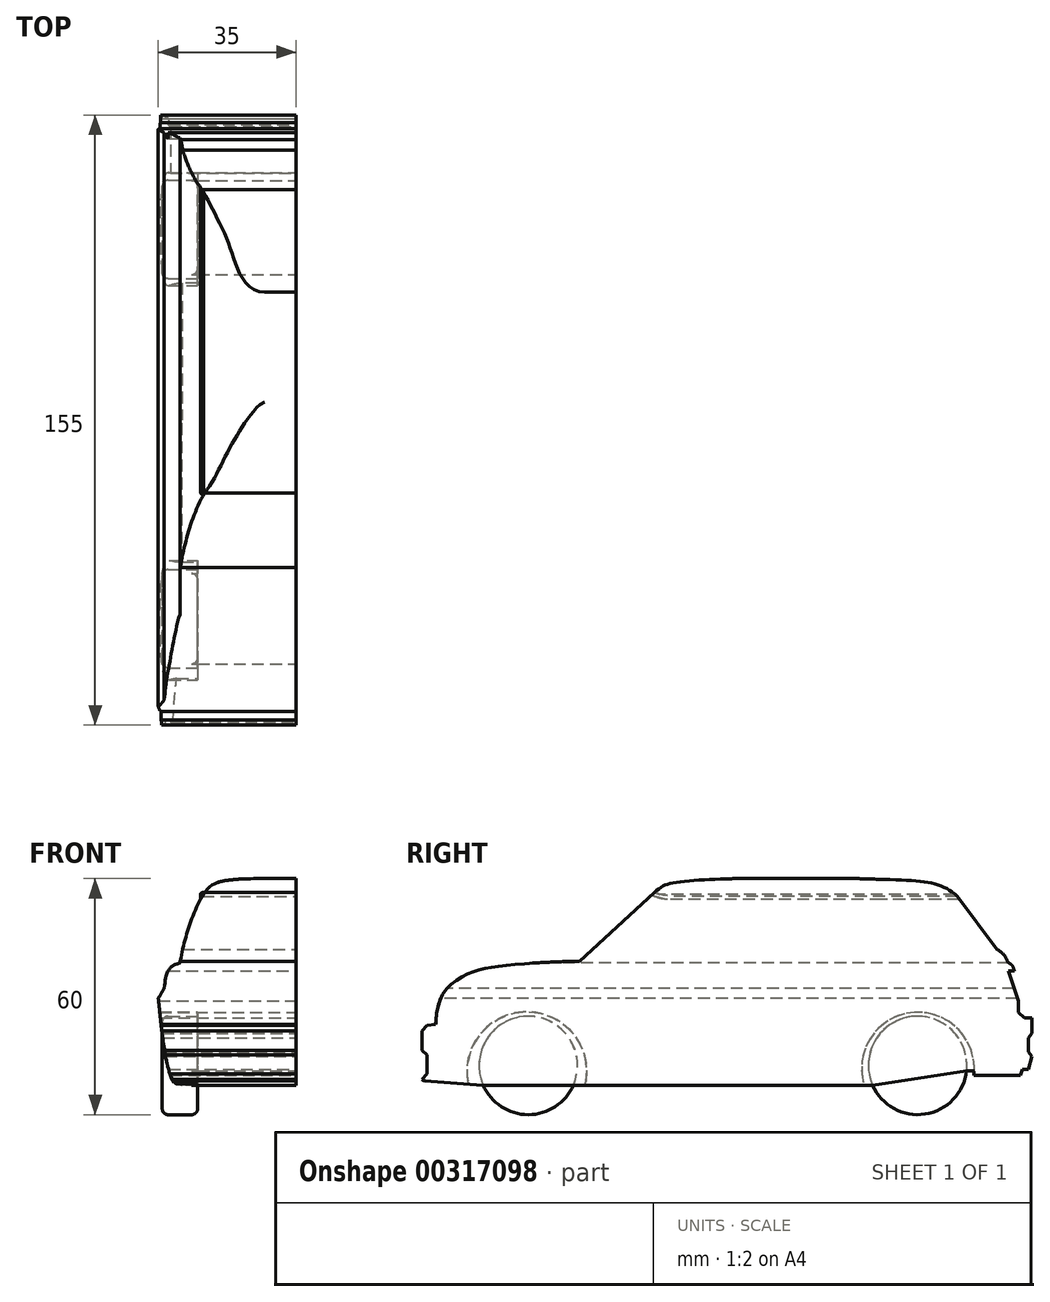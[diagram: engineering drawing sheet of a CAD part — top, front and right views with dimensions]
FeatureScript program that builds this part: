
annotation { "Feature Type Name" : "Feature", "Feature Type Description" : "" }
export const myFeature = defineFeature(function(context is Context, id is Id, definition is map)
    precondition{}
    {
        {
            var Q0;
            Q0=qCreatedBy(makeId("Right.planeOp"),FACE);
            var sketch = newSketch(context, id + "F0", { "sketchPlane" : qUnion([Q0])});
            skLineSegment(sketch, "E0.bottom", {"start": v(-77.5, 0) * mm, "end": v(77.5, 0) * mm});
            skLineSegment(sketch, "E0.top", {"start": v(-77.5, 60) * mm, "end": v(77.5, 60) * mm});
            skLineSegment(sketch, "E0.left", {"start": v(-77.5, 0) * mm, "end": v(-77.5, 60) * mm});
            skLineSegment(sketch, "E0.right", {"start": v(77.5, 0) * mm, "end": v(77.5, 60) * mm});
            skPoint(sketch, "E1", {"position": v(74.5, 10) * mm});
            skPoint(sketch, "E2", {"position": v(75, 11.5) * mm});
            skLineSegment(sketch, "E3", {"start": v(74.5, 10) * mm, "end": v(75, 11.5) * mm});
            skLineSegment(sketch, "E4", {"start": v(76.5, 11.5) * mm, "end": v(75, 11.5) * mm});
            skLineSegment(sketch, "E5", {"start": v(76.5, 11.5) * mm, "end": v(77.5, 14.85) * mm});
            skLineSegment(sketch, "E6", {"start": v(77.5, 14.85) * mm, "end": v(76.5, 16) * mm});
            skLineSegment(sketch, "E7", {"start": v(76.5, 16) * mm, "end": v(76.5, 19.5) * mm});
            skLineSegment(sketch, "E8", {"start": v(76.5, 19.5) * mm, "end": v(77.5, 20.62) * mm});
            skLineSegment(sketch, "E9", {"start": v(77.5, 20.62) * mm, "end": v(77.5, 24.62) * mm});
            skLineSegment(sketch, "E10", {"start": v(77.5, 24.62) * mm, "end": v(75.5, 24.62) * mm});
            skLineSegment(sketch, "E11", {"start": v(75.5, 24.62) * mm, "end": v(74, 25.94) * mm});
            skLineSegment(sketch, "E12", {"start": v(74, 25.94) * mm, "end": v(74, 28.94) * mm});
            skPoint(sketch, "E13", {"position": v(71.5, 36.54) * mm});
            skLineSegment(sketch, "E14", {"start": v(71.5, 36.54) * mm, "end": v(74, 28.94) * mm});
            skLineSegment(sketch, "E15", {"start": v(71.5, 36.54) * mm, "end": v(73, 36.54) * mm});
            skFitSpline(sketch, "E16", {"points": [v(73, 36.54) * mm, v(72.46, 37.9) * mm, v(71.27, 38.84) * mm], "startDerivative": vector(-0.98, 3.1) * mm, "endDerivative": vector(-3.68, 3.33) * mm});
            skPoint(sketch, "E17", {"position": v(68.5, 42) * mm});
            skFitSpline(sketch, "E18", {"points": [v(71.27, 38.84) * mm, v(70.34, 40.67) * mm, v(68.5, 42) * mm], "startDerivative": vector(-1.5, 4.04) * mm, "endDerivative": vector(-4.02, 2.3) * mm});
            skPoint(sketch, "E19", {"position": v(58.5, 55.5) * mm});
            skLineSegment(sketch, "E20", {"start": v(58.5, 55.5) * mm, "end": v(68.5, 42) * mm});
            skPoint(sketch, "E21", {"position": v(32.5, 60) * mm});
            skFitSpline(sketch, "E22", {"points": [v(32.5, 60) * mm, v(52.32, 58.74) * mm, v(58.5, 55.5) * mm], "startDerivative": vector(47.26, -1.79) * mm, "endDerivative": vector(14.98, -13.72) * mm});
            skPoint(sketch, "E23", {"position": v(4.5, 60) * mm});
            skPoint(sketch, "E24", {"position": v(-18.5, 56.5) * mm});
            skFitSpline(sketch, "E25", {"points": [v(4.5, 60) * mm, v(-13.58, 58.93) * mm, v(-18.5, 56.5) * mm], "startDerivative": vector(-24.6, -0.14) * mm, "endDerivative": vector(-14.76, -12.16) * mm});
            skFitSpline(sketch, "E26", {"points": [v(58.5, 55.5) * mm, v(-13.58, 55.5) * mm, v(-18.5, 56.5) * mm], "startDerivative": vector(-273.31, 0) * mm, "endDerivative": vector(-35.98, 14.37) * mm});
            skLineSegment(sketch, "E27", {"start": v(-18.5, 56.5) * mm, "end": v(-37.5, 39) * mm});
            skPoint(sketch, "E28", {"position": v(-74, 23) * mm});
            skFitSpline(sketch, "E29", {"points": [v(-37.5, 39) * mm, v(-58.13, 37.7) * mm, v(-66.06, 35.68) * mm, v(-72.37, 30.31) * mm, v(-74, 23) * mm], "startDerivative": vector(-69.68, -1.64) * mm, "endDerivative": vector(-0.32, -25.11) * mm});
            skLineSegment(sketch, "E30", {"start": v(-74, 23) * mm, "end": v(-76.26, 22.64) * mm});
            skLineSegment(sketch, "E31", {"start": v(-76.26, 22.64) * mm, "end": v(-77.5, 21.31) * mm});
            skLineSegment(sketch, "E32", {"start": v(-77.5, 21.31) * mm, "end": v(-77.5, 16.31) * mm});
            skLineSegment(sketch, "E33", {"start": v(-77.5, 16.31) * mm, "end": v(-76.26, 15.16) * mm});
            skPoint(sketch, "E34", {"position": v(-77.5, 9) * mm});
            skLineSegment(sketch, "E35", {"start": v(-77.5, 9) * mm, "end": v(-76.26, 10.33) * mm});
            skLineSegment(sketch, "E36", {"start": v(-76.26, 10.33) * mm, "end": v(-76.26, 15.16) * mm});
            skLineSegment(sketch, "E37", {"start": v(-77.5, 9) * mm, "end": v(-76.88, 8.62) * mm});
            skPoint(sketch, "E37.endSnap0", {"position": v(-76.88, 9.67) * mm});
            skLineSegment(sketch, "E38", {"start": v(-61.96, 7.5) * mm, "end": v(-76.88, 8.62) * mm});
            skLineSegment(sketch, "E39", {"start": v(-39.04, 7.5) * mm, "end": v(36.96, 7.5) * mm});
            skArc(sketch, "E40", {"start": v(-36.04, 7.5) * mm, "mid": v(-50.7, 26.13) * mm, "end": v(-65.7, 7.78) * mm});
            skPoint(sketch, "E41.second.point", {"position": v(48.41, 0) * mm});
            skPoint(sketch, "E41.third.point", {"position": v(52.15, 24.43) * mm});
            skLineSegment(sketch, "E42", {"start": v(74.5, 10) * mm, "end": v(62.7, 10) * mm});
            skArc(sketch, "E43", {"start": v(62.7, 10) * mm, "mid": v(47.2, 25.95) * mm, "end": v(34.8, 7.5) * mm});
            skLineSegment(sketch, "E44", {"start": v(62.79, 11.13) * mm, "end": v(60.84, 11.13) * mm});
            skFitSpline(sketch, "E45", {"points": [v(-37.5, 39) * mm, v(68.5, 42) * mm], "startDerivative": vector(22.88, -2.64) * mm, "endDerivative": vector(106, 3) * mm});
            skPoint(sketch, "E46", {"position": v(-28, 38.86) * mm});
            skFitSpline(sketch, "E47", {"points": [v(59.1, 54.7) * mm, v(-13.74, 54.51) * mm, v(-19.24, 55.82) * mm], "startDerivative": vector(-279.36, -0.7) * mm, "endDerivative": vector(-40.33, 16.33) * mm});
            skPoint(sketch, "E48", {"position": v(-13, 54.48) * mm});
            skLineSegment(sketch, "E49", {"start": v(-13, 54.48) * mm, "end": v(-28, 38.86) * mm});
            skLineSegment(sketch, "E50", {"start": v(-22.5, 38.96) * mm, "end": v(-9.5, 54.44) * mm});
            skArc(sketch, "E51", {"start": v(-39.04, 7.5) * mm, "mid": v(-50.5, 24.07) * mm, "end": v(-61.96, 7.5) * mm});
            skArc(sketch, "E52", {"start": v(60.84, 11.13) * mm, "mid": v(46.53, 24.86) * mm, "end": v(36.96, 7.5) * mm});
            skLineSegment(sketch, "E53", {"start": v(60.84, 11.13) * mm, "end": v(36.96, 7.5) * mm});
            skLineSegment(sketch, "E54", {"start": v(-39.04, 7.5) * mm, "end": v(-61.96, 7.5) * mm});
            skSolve(sketch);
        }
        {
            var Q0;
            Q0=makeQuery(id+"F0.imprint","IMPRINT",FACE,{"disambiguationData":[TD([[makeQuery(id+"F0.imprint","IMPRINT",EDGE,{"derivedFrom":sQuery(id+"F0.wireOp",EDGE,"E3")}),1.0]])]});
            var Q1;
            {var subQ0=sQuery(id+"F0.wireOp",EDGE,"E22");Q1=makeQuery(id+"F0.imprint","IMPRINT",FACE,{"disambiguationData":[TD([[makeQuery(id+"F0.imprint","IMPRINT",EDGE,{"derivedFrom":subQ0}),-1.0]])]});}
            var Q2;
            {var subQ0=sQuery(id+"F0.wireOp",EDGE,"E41");var subQ1=makeQuery(id+"F0.imprint","INTERSECT",VERTEX,{"derivedFrom":[sQuery(id+"F0.wireOp",EDGE,"E39"),subQ0]});Q2=makeQuery(id+"F0.imprint","IMPRINT",FACE,{"disambiguationData":[TD([[makeQuery(id+"F0.imprint","IMPRINT",EDGE,{"disambiguationData":[TD([[subQ1,-1.0]])],"derivedFrom":subQ0}),1.0]])]});}
            var Q3;
            {var subQ0=sQuery(id+"F0.wireOp",EDGE,"J8efTKUS-d59Y-iMBA-VsDp-mcbD3HcGddpb");var subQ1=makeQuery(id+"F0.imprint","INTERSECT",VERTEX,{"derivedFrom":[subQ0,sQuery(id+"F0.wireOp",EDGE,"E38")]});Q3=makeQuery(id+"F0.imprint","IMPRINT",FACE,{"disambiguationData":[TD([[makeQuery(id+"F0.imprint","IMPRINT",EDGE,{"disambiguationData":[TD([[subQ1,-1.0]])],"derivedFrom":subQ0}),1.0]])]});}
            var Q4;
            {var subQ5=sQuery(id+"F0.wireOp",EDGE,"E49");Q4=makeQuery(id+"F0.imprint","IMPRINT",FACE,{"disambiguationData":[TD([[makeQuery(id+"F0.imprint","IMPRINT",EDGE,{"derivedFrom":subQ5}),-1.0]])]});}
            var Q5;
            {var subQ0=sQuery(id+"F0.wireOp",EDGE,"E49");Q5=makeQuery(id+"F0.imprint","IMPRINT",FACE,{"disambiguationData":[TD([[makeQuery(id+"F0.imprint","IMPRINT",EDGE,{"derivedFrom":subQ0}),1.0]])]});}
            var Q6;
            {var subQ4=sQuery(id+"F0.wireOp",EDGE,"E26");Q6=makeQuery(id+"F0.imprint","IMPRINT",FACE,{"disambiguationData":[TD([[makeQuery(id+"F0.imprint","IMPRINT",EDGE,{"derivedFrom":subQ4}),1.0]])]});}
            var Q7;
            {var subQ5=sQuery(id+"F0.wireOp",EDGE,"E50");Q7=makeQuery(id+"F0.imprint","IMPRINT",FACE,{"disambiguationData":[TD([[makeQuery(id+"F0.imprint","IMPRINT",EDGE,{"derivedFrom":subQ5}),-1.0]])]});}
            extrude(context, id + "F1", {"entities" : qUnion([Q0, Q1, Q2, Q3, Q4, Q5, Q6, Q7]), "oppositeDirection" : true, "depth" : 35 * mm});
        }
        {
            var Q0;
            Q0=qCreatedBy(makeId("Front.planeOp"),FACE);
            var sketch = newSketch(context, id + "F2", { "sketchPlane" : qUnion([Q0])});
            skLineSegment(sketch, "E55.bottom", {"start": v(0, 0) * mm, "end": v(-35, 0) * mm});
            skLineSegment(sketch, "E55.top", {"start": v(0, 65) * mm, "end": v(-35, 65) * mm});
            skLineSegment(sketch, "E55.left", {"start": v(0, 0) * mm, "end": v(0, 65) * mm});
            skLineSegment(sketch, "E55.right", {"start": v(-35, 0) * mm, "end": v(-35, 65) * mm});
            skPoint(sketch, "E56", {"position": v(-35, 29.5) * mm});
            skLineSegment(sketch, "E57", {"start": v(-35, 29.5) * mm, "end": v(-33.5, 32.1) * mm});
            skFitSpline(sketch, "E58", {"points": [v(-33.5, 32.1) * mm, v(-32.18, 37.03) * mm, v(-29.5, 38.5) * mm], "startDerivative": vector(1.24, 9.06) * mm, "endDerivative": vector(5.03, 0.83) * mm});
            skPoint(sketch, "E59", {"position": v(-23.5, 56) * mm});
            skFitSpline(sketch, "E60", {"points": [v(-23.5, 56) * mm, v(-29.5, 38.5) * mm], "startDerivative": vector(-9.23, -14.56) * mm, "endDerivative": vector(-2.83, -16.03) * mm});
            skPoint(sketch, "E61", {"position": v(-8, 60) * mm});
            skFitSpline(sketch, "E62", {"points": [v(-8, 60) * mm, v(-21.58, 58.15) * mm, v(-23.5, 56) * mm], "startDerivative": vector(-44.53, 0) * mm, "endDerivative": vector(-8.43, -11.95) * mm});
            skLineSegment(sketch, "E63", {"start": v(0, 60) * mm, "end": v(-8, 60) * mm});
            skPoint(sketch, "E64", {"position": v(-29, 7.5) * mm});
            skFitSpline(sketch, "E65", {"points": [v(-35, 29.5) * mm, v(-33.18, 14.97) * mm, v(-31.78, 9.67) * mm, v(-30.6, 7.95) * mm, v(-29, 7.5) * mm], "startDerivative": vector(4.83, -44.6) * mm, "endDerivative": vector(12.52, -1.72) * mm});
            skLineSegment(sketch, "E66", {"start": v(-29, 7.5) * mm, "end": v(0, 7.5) * mm});
            skSolve(sketch);
        }
        {
            var Q0;
            {var subQ1=sQuery(id+"F2.wireOp",EDGE,"E55.top");Q0=makeQuery(id+"F2.imprint","IMPRINT",FACE,{"disambiguationData":[TD([[makeQuery(id+"F2.imprint","IMPRINT",EDGE,{"derivedFrom":subQ1}),1.0]])]});}
            var Q1;
            {var subQ2=sQuery(id+"F2.wireOp",EDGE,"E55.bottom");Q1=makeQuery(id+"F2.imprint","IMPRINT",FACE,{"disambiguationData":[TD([[makeQuery(id+"F2.imprint","IMPRINT",EDGE,{"derivedFrom":subQ2}),-1.0]])]});}
            extrude(context, id + "F3", {"entities" : qUnion([Q0, Q1]), "operationType" : NewBodyOperationType.REMOVE, "endBound" : BoundingType.THROUGH_ALL, "oppositeDirection" : true, "depth" : 25 * mm});
        }
        {
            var Q0;
            {var subQ1=sQuery(id+"F2.wireOp",EDGE,"E55.top");Q0=makeQuery(id+"F2.imprint","IMPRINT",FACE,{"disambiguationData":[TD([[makeQuery(id+"F2.imprint","IMPRINT",EDGE,{"derivedFrom":subQ1}),1.0]])]});}
            var Q1;
            {var subQ2=sQuery(id+"F2.wireOp",EDGE,"E55.bottom");Q1=makeQuery(id+"F2.imprint","IMPRINT",FACE,{"disambiguationData":[TD([[makeQuery(id+"F2.imprint","IMPRINT",EDGE,{"derivedFrom":subQ2}),-1.0]])]});}
            extrude(context, id + "F4", {"entities" : qUnion([Q0, Q1]), "operationType" : NewBodyOperationType.REMOVE, "endBound" : BoundingType.THROUGH_ALL, "depth" : 25 * mm});
        }
        {
            var Q0;
            {var subQ3=sQuery(id+"F0.wireOp",EDGE,"E40");Q0=makeQuery(id+"F0.imprint","IMPRINT",FACE,{"disambiguationData":[TD([[makeQuery(id+"F0.imprint","IMPRINT",EDGE,{"derivedFrom":subQ3}),1.0]])]});}
            var Q1;
            Q1=makeQuery(id+"F0.imprint","IMPRINT",FACE,{"disambiguationData":[TD([[makeQuery(id+"F0.imprint","IMPRINT",EDGE,{"derivedFrom":sQuery(id+"F0.wireOp",EDGE,"E51")}),1.0]])]});
            var Q2;
            {var subQ4=sQuery(id+"F0.wireOp",EDGE,"E44");Q2=makeQuery(id+"F0.imprint","IMPRINT",FACE,{"disambiguationData":[TD([[makeQuery(id+"F0.imprint","IMPRINT",EDGE,{"derivedFrom":subQ4}),-1.0]])]});}
            var Q3;
            Q3=makeQuery(id+"F0.imprint","IMPRINT",FACE,{"disambiguationData":[TD([[makeQuery(id+"F0.imprint","IMPRINT",EDGE,{"derivedFrom":sQuery(id+"F0.wireOp",EDGE,"E52")}),1.0]])]});
            extrude(context, id + "F5", {"entities" : qUnion([Q0, Q1, Q2, Q3]), "operationType" : NewBodyOperationType.ADD, "oppositeDirection" : true, "depth" : 25 * mm});
        }
        {
            var Q0;
            Q0=makeQuery(id+"F5.opExtrude","CAP_FACE",FACE,{"disambiguationData":[OSD([sQuery(id+"F0.wireOp",EDGE,"E38"),sQuery(id+"F0.wireOp",EDGE,"E39"),sQuery(id+"F0.wireOp",EDGE,"E40"),sQuery(id+"F0.wireOp",EDGE,"E54")])],"isStart":false});
            var sketch = newSketch(context, id + "F6", { "sketchPlane" : qUnion([Q0])});
            skCircle(sketch, "E67", {"center": v(50.5, 12.5) * mm, "radius": 12.5 * mm});
            skPoint(sketch, "E67.first.point", {"position": v(39.04, 7.5) * mm});
            skPoint(sketch, "E67.second.point", {"position": v(61.96, 7.5) * mm});
            skPoint(sketch, "E67.third.point", {"position": v(50.75, 25) * mm});
            skSolve(sketch);
        }
        {
            var Q0;
            Q0 = qSketchRegion(id + "F6", true);
            extrude(context, id + "F7", {"entities" : qUnion([Q0]), "operationType" : NewBodyOperationType.ADD, "depth" : 9 * mm});
        }
        {
            var Q0;
            Q0=makeQuery(id+"F5.opExtrude","CAP_FACE",FACE,{"disambiguationData":[OSD([sQuery(id+"F0.wireOp",EDGE,"E39"),sQuery(id+"F0.wireOp",EDGE,"E43"),sQuery(id+"F0.wireOp",EDGE,"E44"),sQuery(id+"F0.wireOp",EDGE,"E53")])],"isStart":false});
            var sketch = newSketch(context, id + "F8", { "sketchPlane" : qUnion([Q0])});
            skCircle(sketch, "E68", {"center": v(-48.41, 12.5) * mm, "radius": 12.5 * mm});
            skPoint(sketch, "E68.first.point", {"position": v(-60.84, 11.13) * mm});
            skPoint(sketch, "E68.second.point", {"position": v(-36.96, 7.5) * mm});
            skPoint(sketch, "E68.third.point", {"position": v(-48.36, 0) * mm});
            skSolve(sketch);
        }
        {
            var Q0;
            Q0 = qSketchRegion(id + "F8", true);
            extrude(context, id + "F9", {"entities" : qUnion([Q0]), "operationType" : NewBodyOperationType.ADD, "depth" : 9 * mm});
        }
        {
            var Q0;
            Q0=makeQuery(id+"F9.opExtrude","CAP_EDGE",EDGE,{"disambiguationData":[OSD([sQuery(id+"F8.wireOp",EDGE,"E68")])],"isStart":false});
            var Q1;
            {var subQ0=sQuery(id+"F8.wireOp",EDGE,"E68");Q1=makeQuery(id+"F9.boolean.opBoolean","SPLIT",EDGE,{"disambiguationData":[topologyDisambiguationEdgeConnected([makeQuery(id+"F9.opExtrude","CAP_FACE",FACE,{"disambiguationData":[OSD([subQ0])],"isStart":true})])],"derivedFrom":makeQuery(id+"F9.opExtrude","CAP_EDGE",EDGE,{"disambiguationData":[OSD([subQ0])],"isStart":true})});}
            var Q2;
            {var subQ0=sQuery(id+"F6.wireOp",EDGE,"E67");Q2=makeQuery(id+"F7.boolean.opBoolean","SPLIT",EDGE,{"disambiguationData":[topologyDisambiguationEdgeConnected([makeQuery(id+"F7.opExtrude","CAP_FACE",FACE,{"disambiguationData":[OSD([subQ0])],"isStart":true})])],"derivedFrom":makeQuery(id+"F7.opExtrude","CAP_EDGE",EDGE,{"disambiguationData":[OSD([subQ0])],"isStart":true})});}
            var Q3;
            Q3=makeQuery(id+"F7.opExtrude","CAP_EDGE",EDGE,{"disambiguationData":[OSD([sQuery(id+"F6.wireOp",EDGE,"E67")])],"isStart":false});
            fillet(context, id + "F10", {"entities" : qUnion([Q0, Q1, Q2, Q3]), "radius" : 1.5 * mm, "tangentPropagation" : true, "allowEdgeOverflow" : false});
        }
        {
            var Q0;
            {var subQ4=sQuery(id+"F0.wireOp",EDGE,"E26");Q0=makeQuery(id+"F0.imprint","IMPRINT",FACE,{"disambiguationData":[TD([[makeQuery(id+"F0.imprint","IMPRINT",EDGE,{"derivedFrom":subQ4}),1.0]])]});}
            extrude(context, id + "F11", {"entities" : qUnion([Q0]), "operationType" : NewBodyOperationType.ADD, "oppositeDirection" : true, "depth" : 24.3 * mm});
        }
        {
            var Q0;
            Q0=makeQuery(id+"F11.opExtrude","CAP_EDGE",EDGE,{"disambiguationData":[OSD([sQuery(id+"F0.wireOp",EDGE,"E27")])],"isStart":false});
            fillet(context, id + "F12", {"entities" : qUnion([Q0]), "radius" : 1.1 * mm, "tangentPropagation" : true, "allowEdgeOverflow" : false});
        }
    });
